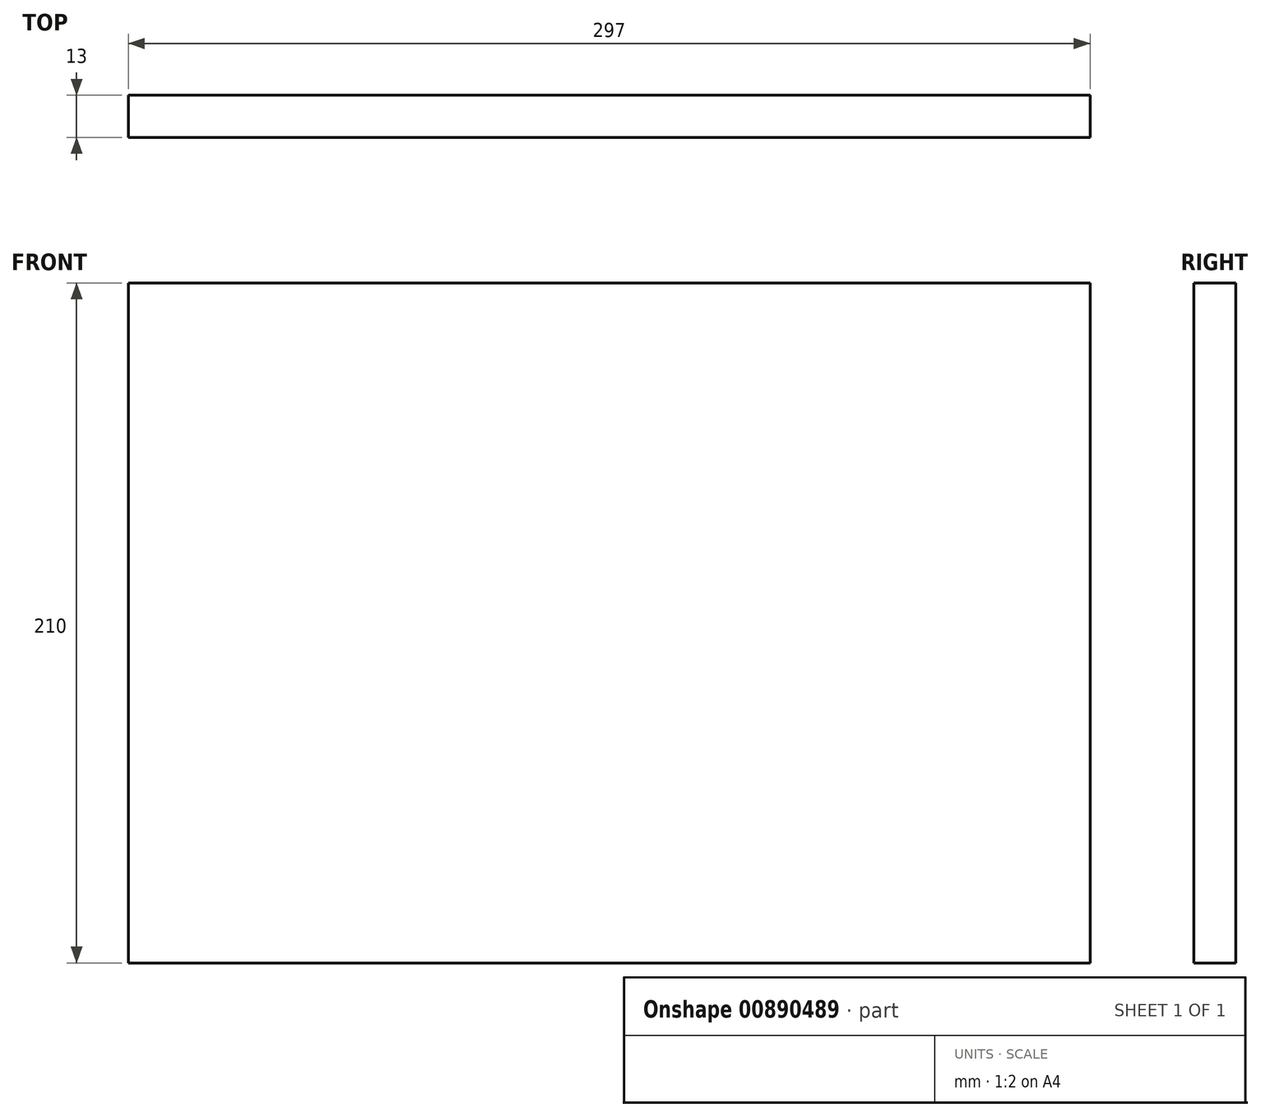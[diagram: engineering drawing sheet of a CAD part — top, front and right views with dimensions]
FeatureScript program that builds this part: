
annotation { "Feature Type Name" : "Feature", "Feature Type Description" : "" }
export const myFeature = defineFeature(function(context is Context, id is Id, definition is map)
    precondition{}
    {
        {
            var Q0;
            Q0=qCreatedBy(makeId("Front.planeOp"),FACE);
            var sketch = newSketch(context, id + "F0", { "sketchPlane" : qUnion([Q0])});
            skLineSegment(sketch, "E0.bottom", {"start": v(-123.09, 100.95) * mm, "end": v(173.91, 100.95) * mm});
            skLineSegment(sketch, "E0.top", {"start": v(-123.09, -109.05) * mm, "end": v(173.91, -109.05) * mm});
            skLineSegment(sketch, "E0.left", {"start": v(-123.09, 100.95) * mm, "end": v(-123.09, -109.05) * mm});
            skLineSegment(sketch, "E0.right", {"start": v(173.91, 100.95) * mm, "end": v(173.91, -109.05) * mm});
            skSolve(sketch);
        }
        {
            var Q0;
            Q0=makeQuery(id+"F0.imprint","IMPRINT",FACE,{"disambiguationData":[TD([[makeQuery(id+"F0.imprint","IMPRINT",EDGE,{"derivedFrom":sQuery(id+"F0.wireOp",EDGE,"E0.bottom")}),-1.0]])]});
            extrude(context, id + "F1", {"entities" : qUnion([Q0]), "depth" : 13 * mm, "offsetDistance" : 25 * mm});
        }
    });
